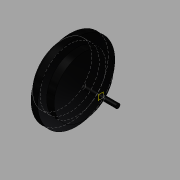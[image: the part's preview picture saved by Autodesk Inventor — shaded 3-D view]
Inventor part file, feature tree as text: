
AUTODESK INVENTOR PART (.ipt)
format: ipt  version: 2015 (Build 190159000, 159)  size: 108,032 bytes
history: native  units: in
note: dims shown in document units (in); Inventor stores cm internally (conversion verified against a paired STEP export)
features: other x3, sketch x3, plane x1
ambient origin geometry x8: Origin, YZ Plane, XZ Plane, XY Plane, X Axis, Y Axis, Z Axis, Center Point
bodies: Solid1 (feature_tree)
feature tree (7):
  other  "rueda_MIR3.ipt"
  other  "Solid1::rueda_MIR3.ipt"
  other  "TaggingFeature1"
  sketch  "Sketch2"  dims[d0=0.3937in]
  sketch  "Sketch3"
  sketch  "Sketch7"
  plane  "Work Plane1"
